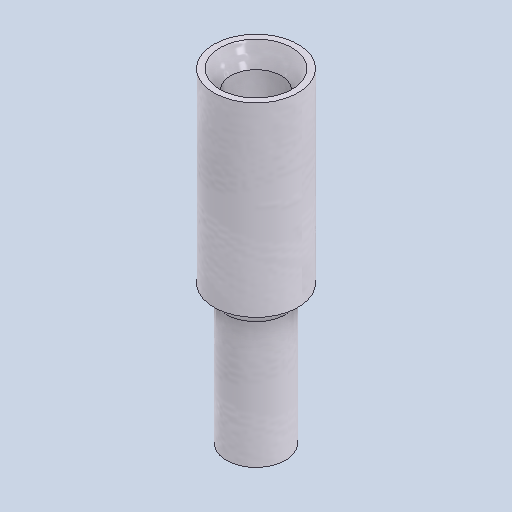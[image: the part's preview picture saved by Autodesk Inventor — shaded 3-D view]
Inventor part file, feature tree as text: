
AUTODESK INVENTOR PART (.ipt)
format: ipt  version: 2022 (Build 260153070, 153G)  size: 134,144 bytes
history: native  units: mm
features: revolve x1, sketch x1
ambient origin geometry x8: Origin, YZ Plane, XZ Plane, XY Plane, X Axis, Y Axis, Z Axis, Center Point
bodies: Solid1 (feature_tree)
feature tree (2):
  revolve  "Revolution1"  [1 undecoded]
  sketch  "Sketch1"  dims[d1=10.5mm d2=2.45mm d3=3.5mm d4=30.0deg d5=2.1mm d6=135.0deg d7=0.5mm d8=27.0mm d9=90.0deg]
note: 1 required parameter value undecoded (feature->parameter linkage not recoverable at this tier; creation-order binding heuristic only, values carry confidence <= 0.55)
